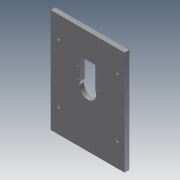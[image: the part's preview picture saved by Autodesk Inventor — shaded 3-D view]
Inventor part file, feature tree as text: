
AUTODESK INVENTOR PART (.ipt)
format: ipt  version: 2011 (Build 150239000, 239)  size: 495,104 bytes
history: native  units: in
note: dims shown in document units (in); Inventor stores cm internally (conversion verified against a paired STEP export)
features: extrude x49, sketch x49, fillet x2
ambient origin geometry x8: Origin, YZ Plane, XZ Plane, XY Plane, X Axis, Y Axis, Z Axis, Center Point
bodies: Solid1 (feature_tree)
feature tree (100):
  extrude  "Extrusion1"  Depth=4.0in
  extrude  "Extrusion2"  Depth=2.16in
  extrude  "Extrusion3"  Depth=1.7655in
  extrude  "Extrusion4"  Depth=0.029in TaperAngle=0.0deg
  extrude  "Extrusion5"  Depth=2.36in
  fillet  "Fillet1"  Radius=2.56in
  extrude  "Extrusion6"  Depth=0.125in
  extrude  "Extrusion7"  Depth=0.262in TaperAngle=0.0deg
  extrude  "Extrusion8"  Depth=0.029in TaperAngle=0.0deg
  extrude  "Extrusion9"  Depth=0.156in
  extrude  "Extrusion10"  Depth=0.5in TaperAngle=0.0deg
  extrude  "Extrusion11"  Depth=0.5in TaperAngle=0.0deg
  extrude  "Extrusion12"  Depth=1.875in TaperAngle=0.0deg
  extrude  "Extrusion13"  Depth=2.125in TaperAngle=0.0deg
  sketch  "Sketch14"  dims[d44=2.125in d45=0.0in d46=2.125in d47=0.0in]
  sketch  "Sketch15"  dims[d48=2.125in d49=0.0in d50=1.875in d51=0.0in]
  sketch  "Sketch16"  dims[d52=2.125in d53=0.0in d54=2.125in d55=0.0in]
  sketch  "Sketch17"  dims[d56=1.875in d57=0.0in d58=1.875in d59=0.0in]
  extrude  "Extrusion14"  Depth=2.125in TaperAngle=0.0deg
  extrude  "Extrusion15"  Depth=1.875in TaperAngle=0.0deg
  extrude  "Extrusion16"  Depth=2.125in TaperAngle=0.0deg
  extrude  "Extrusion17"  Depth=1.875in TaperAngle=0.0deg
  extrude  "Extrusion18"  Depth=2.125in TaperAngle=0.0deg
  extrude  "Extrusion19"  Depth=6.248in TaperAngle=0.0deg
  extrude  "Extrusion20"  Depth=1.281in
  extrude  "Extrusion21"  Depth=7.0in TaperAngle=0.0deg
  extrude  "Extrusion22"  Depth=2.0in
  extrude  "Extrusion23"  Depth=4.0in
  extrude  "Extrusion24"  Depth=2.0in
  extrude  "Extrusion25"  Depth=1.0in TaperAngle=0.0deg
  extrude  "Extrusion26"  Depth=0.25in
  extrude  "Extrusion27"  Depth=0.25in TaperAngle=0.0deg
  extrude  "Extrusion28"  Depth=0.25in TaperAngle=0.0deg
  extrude  "Extrusion29"  Depth=0.875in
  extrude  "Extrusion30"  Depth=0.5in TaperAngle=0.0deg
  extrude  "Extrusion31"  Depth=0.875in
  extrude  "Extrusion32"  Depth=0.5in TaperAngle=0.0deg
  extrude  "Extrusion33"  Depth=2.0in
  extrude  "Extrusion34"  Depth=4.0in
  fillet  "Fillet2"  Radius=1.0in
  extrude  "Extrusion35"  Depth=0.75in TaperAngle=0.0deg
  extrude  "Extrusion36"  Depth=0.9055in
  extrude  "Extrusion37"  Depth=0.8268in
  extrude  "Extrusion38"  Depth=0.75in TaperAngle=0.0deg
  extrude  "Extrusion39"  Depth=0.2559in
  extrude  "Extrusion40"  Depth=0.315in
  extrude  "Extrusion41"  Depth=1.063in
  extrude  "Extrusion42"  Depth=1.0in TaperAngle=0.0deg
  extrude  "Extrusion43"  Depth=0.125in TaperAngle=0.0deg
  extrude  "Extrusion44"  [1 undecoded]
  extrude  "Extrusion45"  [1 undecoded]
  extrude  "Extrusion46"  [1 undecoded]
  extrude  "Extrusion47"  [1 undecoded]
  extrude  "Extrusion48"  [1 undecoded]
  extrude  "Extrusion49"  [1 undecoded]
  sketch  "Sketch1"  dims[d0=4.0in d1=4.0in]
  sketch  "Sketch2"  dims[d2=0.029in d3=0.0in d4=2.16in]
  sketch  "Sketch3"  dims[d5=0.029in d6=0.0in d7=1.7655in]
  sketch  "Sketch4"  dims[d8=0.156in d9=0.029in d10=0.0in]
  sketch  "Sketch5"  dims[d11=0.029in d12=0.0in d13=2.36in d14=2.56in]
  sketch  "Sketch6"  dims[d15=0.262in d16=0.0in d17=0.125in]
  sketch  "Sketch7"  dims[d18=0.362in d19=0.0in d20=0.262in d21=0.0in]
  sketch  "Sketch8"  dims[d22=0.1in d23=0.0in d24=0.029in d25=0.0in]
  sketch  "Sketch9"  dims[d26=1.594in d27=0.156in]
  sketch  "Sketch10"  dims[d28=0.029in d29=0.0in d30=0.5in d31=0.0in]
  sketch  "Sketch11"  dims[d32=0.75in d33=0.0in d34=0.5in d35=0.0in]
  sketch  "Sketch12"  dims[d36=2.125in d37=0.0in d38=1.875in d39=0.0in]
  sketch  "Sketch13"  dims[d40=1.875in d41=0.0in d42=2.125in d43=0.0in]
  sketch  "Sketch18"  dims[d60=2.125in d61=0.0in d62=2.125in d63=0.0in]
  sketch  "Sketch19"  dims[d64=0.875in d65=0.0in d66=6.248in d67=0.0in]
  sketch  "Sketch20"  dims[d68=7.0in d69=0.0in d70=1.281in]
  sketch  "Sketch21"  dims[d71=3.188in d72=7.0in d73=0.0in]
  sketch  "Sketch22"  dims[d74=0.25in d75=0.0in d76=2.0in]
  sketch  "Sketch23"  dims[d77=2.0in d78=4.0in]
  sketch  "Sketch24"  dims[d79=1.0in d80=0.0in d81=2.0in]
  sketch  "Sketch25"  dims[d82=1.0in d83=1.0in d84=0.0in]
  sketch  "Sketch26"  dims[d85=0.5in d86=0.25in]
  sketch  "Sketch27"  dims[d87=0.25in d88=0.25in d89=0.0in]
  sketch  "Sketch28"  dims[d90=0.25in d91=0.0in d92=0.25in d93=0.0in]
  sketch  "Sketch29"  dims[d94=0.656in d95=0.875in]
  sketch  "Sketch30"  dims[d96=0.5in d97=0.0in d98=0.5in d99=0.0in]
  sketch  "Sketch31"  dims[d100=0.875in d101=0.875in]
  sketch  "Sketch32"  dims[d102=0.5in d103=0.0in d104=0.5in d105=0.0in]
  sketch  "Sketch33"  dims[d106=2.0in d107=2.0in]
  sketch  "Sketch34"  dims[d108=4.0in d109=4.0in d110=1.0in d111=0.0in]
  sketch  "Sketch35"  dims[d112=0.25in d113=0.0in d114=0.75in d115=0.0in]
  sketch  "Sketch36"  dims[d116=0.75in d117=0.0in d118=0.9055in]
  sketch  "Sketch37"  dims[d119=0.4134in d120=0.8268in]
  sketch  "Sketch38"  dims[d121=1.378in d122=0.75in d123=0.0in]
  sketch  "Sketch39"  dims[d124=0.5315in d125=0.2559in]
  sketch  "Sketch40"  dims[d126=0.315in d127=0.315in]
  sketch  "Sketch41"  dims[d128=1.063in d129=1.063in]
  sketch  "Sketch42"  dims[d130=0.0787in d131=1.0in d132=0.0in]
  sketch  "Sketch43"  dims[d133=0.125in d134=0.0in d135=0.125in d136=0.0in]
  sketch  "Sketch44"
  sketch  "Sketch45"
  sketch  "Sketch46"
  sketch  "Sketch47"
  sketch  "Sketch49"
  sketch  "Sketch50"
note: 6 required parameter values undecoded (feature->parameter linkage not recoverable at this tier; creation-order binding heuristic only, values carry confidence <= 0.55)
